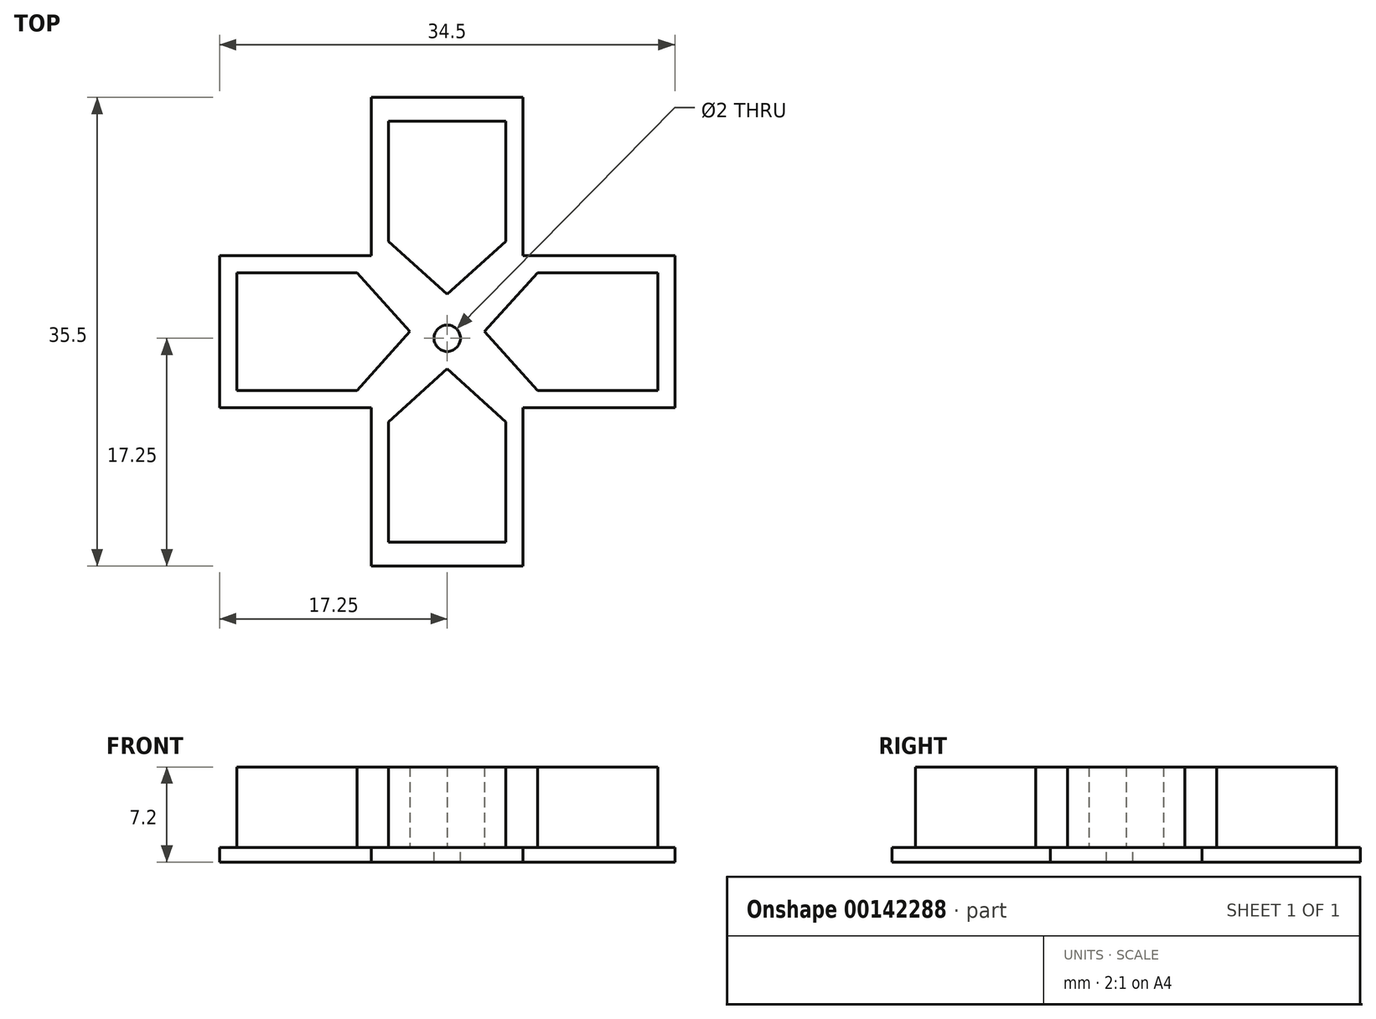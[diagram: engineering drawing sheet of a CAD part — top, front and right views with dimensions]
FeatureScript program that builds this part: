
annotation { "Feature Type Name" : "Feature", "Feature Type Description" : "" }
export const myFeature = defineFeature(function(context is Context, id is Id, definition is map)
    precondition{}
    {
        {
            var Q0;
            Q0=qCreatedBy(makeId("Top.planeOp"),FACE);
            var sketch = newSketch(context, id + "F0", { "sketchPlane" : qUnion([Q0])});
            skLineSegment(sketch, "E0", {"start": v(-23, 11.5) * mm, "end": v(-23, 0) * mm});
            skLineSegment(sketch, "E1", {"start": v(-23, 0) * mm, "end": v(-11.5, 0) * mm});
            skLineSegment(sketch, "E2", {"start": v(-11.5, 0) * mm, "end": v(-11.5, -12) * mm});
            skLineSegment(sketch, "E3", {"start": v(-11.5, -12) * mm, "end": v(0, -12) * mm});
            skLineSegment(sketch, "E4", {"start": v(0, -12) * mm, "end": v(0, 0) * mm});
            skLineSegment(sketch, "E5", {"start": v(0, 0) * mm, "end": v(11.5, 0) * mm});
            skLineSegment(sketch, "E6", {"start": v(11.5, 0) * mm, "end": v(11.5, 11.5) * mm});
            skLineSegment(sketch, "E7", {"start": v(11.5, 11.5) * mm, "end": v(0, 11.5) * mm});
            skLineSegment(sketch, "E8", {"start": v(0, 11.5) * mm, "end": v(0, 23.5) * mm});
            skLineSegment(sketch, "E9", {"start": v(0, 23.5) * mm, "end": v(-11.5, 23.5) * mm});
            skLineSegment(sketch, "E10", {"start": v(-11.5, 23.5) * mm, "end": v(-11.5, 11.5) * mm});
            skLineSegment(sketch, "E11", {"start": v(-11.5, 11.5) * mm, "end": v(-23, 11.5) * mm});
            skSolve(sketch);
        }
        {
            var Q0;
            Q0 = qSketchRegion(id + "F0", true);
            extrude(context, id + "F1", {"entities" : qUnion([Q0]), "depth" : 1.1 * mm});
        }
        {
            var Q0;
            Q0=makeQuery(id+"F1.opExtrude","CAP_FACE",FACE,{"disambiguationData":[OSD([sQuery(id+"F0.wireOp",EDGE,"E0"),sQuery(id+"F0.wireOp",EDGE,"E1"),sQuery(id+"F0.wireOp",EDGE,"E2"),sQuery(id+"F0.wireOp",EDGE,"E3"),sQuery(id+"F0.wireOp",EDGE,"E4"),sQuery(id+"F0.wireOp",EDGE,"E5"),sQuery(id+"F0.wireOp",EDGE,"E6"),sQuery(id+"F0.wireOp",EDGE,"E7"),sQuery(id+"F0.wireOp",EDGE,"E8"),sQuery(id+"F0.wireOp",EDGE,"E9"),sQuery(id+"F0.wireOp",EDGE,"E10"),sQuery(id+"F0.wireOp",EDGE,"E11")])],"isStart":false});
            var sketch = newSketch(context, id + "F2", { "sketchPlane" : qUnion([Q0])});
            skLineSegment(sketch, "E12", {"start": v(-10.2, 21.7) * mm, "end": v(-1.3, 21.7) * mm});
            skLineSegment(sketch, "E13", {"start": v(-1.3, 21.7) * mm, "end": v(-1.3, 12.6) * mm});
            skLineSegment(sketch, "E14", {"start": v(-1.3, 12.6) * mm, "end": v(-5.75, 8.58) * mm});
            skLineSegment(sketch, "E15", {"start": v(-5.75, 8.58) * mm, "end": v(-10.2, 12.6) * mm});
            skLineSegment(sketch, "E16", {"start": v(-10.2, 12.6) * mm, "end": v(-10.2, 21.7) * mm});
            skLineSegment(sketch, "E17", {"start": v(-10.2, 12.6) * mm, "end": v(-1.3, 12.6) * mm});
            skCircle(sketch, "E18", {"center": v(-5.75, 5.25) * mm, "radius": 1 * mm});
            skLineSegment(sketch, "E19", {"start": v(-21.7, 10.2) * mm, "end": v(-21.7, 1.3) * mm});
            skLineSegment(sketch, "E20", {"start": v(-21.7, 1.3) * mm, "end": v(-12.6, 1.3) * mm});
            skLineSegment(sketch, "E21", {"start": v(-12.6, 1.3) * mm, "end": v(-8.58, 5.75) * mm});
            skLineSegment(sketch, "E22", {"start": v(-8.58, 5.75) * mm, "end": v(-12.6, 10.2) * mm});
            skLineSegment(sketch, "E23", {"start": v(-12.6, 10.2) * mm, "end": v(-21.7, 10.2) * mm});
            skLineSegment(sketch, "E24", {"start": v(-12.6, 10.2) * mm, "end": v(-12.6, 1.3) * mm});
            skLineSegment(sketch, "E25", {"start": v(10.2, 10.2) * mm, "end": v(10.2, 1.3) * mm});
            skLineSegment(sketch, "E26", {"start": v(10.2, 1.3) * mm, "end": v(1.1, 1.3) * mm});
            skLineSegment(sketch, "E27", {"start": v(1.1, 1.3) * mm, "end": v(-2.92, 5.75) * mm});
            skLineSegment(sketch, "E28", {"start": v(-2.92, 5.75) * mm, "end": v(1.1, 10.2) * mm});
            skLineSegment(sketch, "E29", {"start": v(1.1, 10.2) * mm, "end": v(10.2, 10.2) * mm});
            skLineSegment(sketch, "E30", {"start": v(1.1, 10.2) * mm, "end": v(1.1, 1.3) * mm});
            skLineSegment(sketch, "E31", {"start": v(-10.2, -1.1) * mm, "end": v(-10.2, -10.2) * mm});
            skLineSegment(sketch, "E32", {"start": v(-10.2, -10.2) * mm, "end": v(-1.3, -10.2) * mm});
            skLineSegment(sketch, "E33", {"start": v(-1.3, -10.2) * mm, "end": v(-1.3, -1.1) * mm});
            skLineSegment(sketch, "E34", {"start": v(-1.3, -1.1) * mm, "end": v(-5.75, 2.92) * mm});
            skLineSegment(sketch, "E35", {"start": v(-5.75, 2.92) * mm, "end": v(-10.2, -1.1) * mm});
            skLineSegment(sketch, "E36", {"start": v(-1.3, -1.1) * mm, "end": v(-10.2, -1.1) * mm});
            skSolve(sketch);
        }
        {
            var Q0;
            Q0=makeQuery(id+"F2.imprint","IMPRINT",FACE,{"disambiguationData":[TD([[makeQuery(id+"F2.imprint","IMPRINT",EDGE,{"derivedFrom":sQuery(id+"F2.wireOp",EDGE,"E19")}),1.0]])]});
            var Q1;
            Q1=makeQuery(id+"F2.imprint","IMPRINT",FACE,{"disambiguationData":[TD([[makeQuery(id+"F2.imprint","IMPRINT",EDGE,{"derivedFrom":sQuery(id+"F2.wireOp",EDGE,"E21")}),1.0]])]});
            var Q2;
            Q2=makeQuery(id+"F2.imprint","IMPRINT",FACE,{"disambiguationData":[TD([[makeQuery(id+"F2.imprint","IMPRINT",EDGE,{"derivedFrom":sQuery(id+"F2.wireOp",EDGE,"E34")}),1.0]])]});
            var Q3;
            Q3=makeQuery(id+"F2.imprint","IMPRINT",FACE,{"disambiguationData":[TD([[makeQuery(id+"F2.imprint","IMPRINT",EDGE,{"derivedFrom":sQuery(id+"F2.wireOp",EDGE,"E31")}),1.0]])]});
            var Q4;
            Q4=makeQuery(id+"F2.imprint","IMPRINT",FACE,{"disambiguationData":[TD([[makeQuery(id+"F2.imprint","IMPRINT",EDGE,{"derivedFrom":sQuery(id+"F2.wireOp",EDGE,"E25")}),-1.0]])]});
            var Q5;
            Q5=makeQuery(id+"F2.imprint","IMPRINT",FACE,{"disambiguationData":[TD([[makeQuery(id+"F2.imprint","IMPRINT",EDGE,{"derivedFrom":sQuery(id+"F2.wireOp",EDGE,"E27")}),-1.0]])]});
            var Q6;
            Q6=makeQuery(id+"F2.imprint","IMPRINT",FACE,{"disambiguationData":[TD([[makeQuery(id+"F2.imprint","IMPRINT",EDGE,{"derivedFrom":sQuery(id+"F2.wireOp",EDGE,"E14")}),-1.0]])]});
            var Q7;
            Q7=makeQuery(id+"F2.imprint","IMPRINT",FACE,{"disambiguationData":[TD([[makeQuery(id+"F2.imprint","IMPRINT",EDGE,{"derivedFrom":sQuery(id+"F2.wireOp",EDGE,"E12")}),-1.0]])]});
            extrude(context, id + "F3", {"entities" : qUnion([Q0, Q1, Q2, Q3, Q4, Q5, Q6, Q7]), "operationType" : NewBodyOperationType.ADD, "depth" : 6.1 * mm});
        }
        {
            var Q0;
            Q0=makeQuery(id+"F2.imprint","IMPRINT",FACE,{"disambiguationData":[TD([[makeQuery(id+"F2.imprint","IMPRINT",EDGE,{"derivedFrom":sQuery(id+"F2.wireOp",EDGE,"E18")}),1.0]])]});
            extrude(context, id + "F4", {"entities" : qUnion([Q0]), "operationType" : NewBodyOperationType.REMOVE, "endBound" : BoundingType.THROUGH_ALL, "oppositeDirection" : true, "depth" : 25 * mm});
        }
    });
